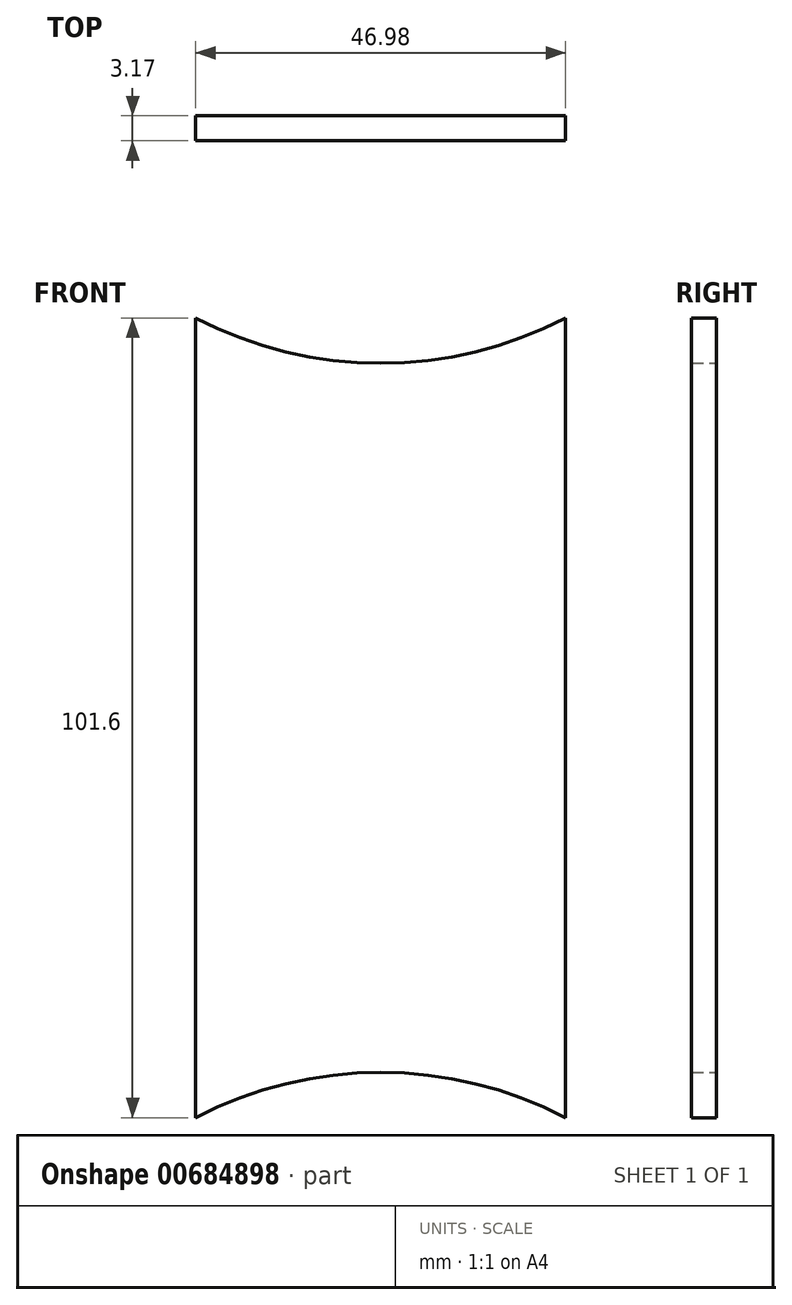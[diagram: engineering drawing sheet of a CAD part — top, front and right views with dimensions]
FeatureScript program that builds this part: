
annotation { "Feature Type Name" : "Feature", "Feature Type Description" : "" }
export const myFeature = defineFeature(function(context is Context, id is Id, definition is map)
    precondition{}
    {
        {
            var Q0;
            Q0=qCreatedBy(makeId("Front.planeOp"),FACE);
            var sketch = newSketch(context, id + "F0", { "sketchPlane" : qUnion([Q0])});
            skLineSegment(sketch, "E0", {"start": v(0, 60.46) * mm, "end": v(0, -115.44) * mm, "construction": true});
            skLineSegment(sketch, "E1", {"start": v(23.5, 50.8) * mm, "end": v(23.5, -50.8) * mm});
            skLineSegment(sketch, "E2", {"start": v(-52.24, 50.8) * mm, "end": v(53, 50.8) * mm, "construction": true});
            skLineSegment(sketch, "E3", {"start": v(-49.56, 0) * mm, "end": v(74.1, 0) * mm, "construction": true});
            skLineSegment(sketch, "E4.MirrorCS", {"start": v(-52.24, -50.8) * mm, "end": v(53, -50.8) * mm, "construction": true});
            skLineSegment(sketch, "E5.MirrorCS", {"start": v(-23.5, 50.8) * mm, "end": v(-23.5, -50.8) * mm});
            skArc(sketch, "E6", {"start": v(23.5, -50.8) * mm, "mid": v(0, -45.04) * mm, "end": v(-23.5, -50.8) * mm});
            skArc(sketch, "E7.MirrorCS", {"start": v(23.5, 50.8) * mm, "mid": v(0, 45.04) * mm, "end": v(-23.5, 50.8) * mm});
            skSolve(sketch);
        }
        {
            var Q0;
            Q0 = qSketchRegion(id + "F0", true);
            extrude(context, id + "F1", {"entities" : qUnion([Q0]), "depth" : 3.17 * mm, "offsetDistance" : 25.4 * mm});
        }
    });
